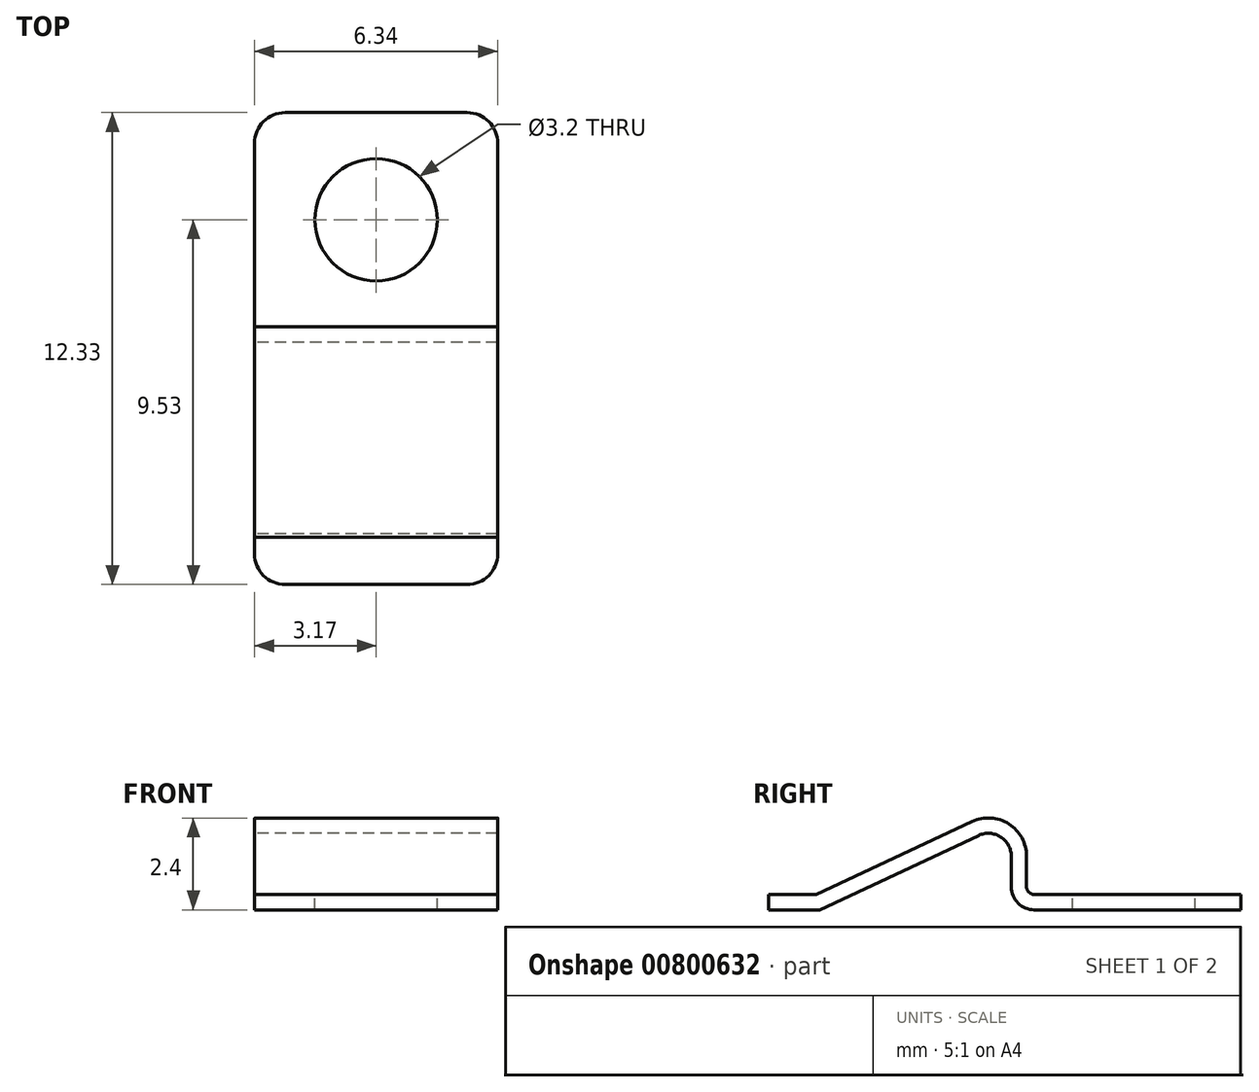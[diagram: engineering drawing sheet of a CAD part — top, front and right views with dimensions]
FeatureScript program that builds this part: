
annotation { "Feature Type Name" : "Feature", "Feature Type Description" : "" }
export const myFeature = defineFeature(function(context is Context, id is Id, definition is map)
    precondition{}
    {
        {
            var Q0;
            Q0=qCreatedBy(makeId("Right.planeOp"),FACE);
            var sketch = newSketch(context, id + "F0", { "sketchPlane" : qUnion([Q0])});
            skLineSegment(sketch, "E0", {"start": v(0, 0) * mm, "end": v(-5.4, 0) * mm});
            skLineSegment(sketch, "E1", {"start": v(-6, 0.6) * mm, "end": v(-6, 1.4) * mm});
            skLineSegment(sketch, "E2", {"start": v(-6.85, 1.94) * mm, "end": v(-11, 0) * mm});
            skLineSegment(sketch, "E3", {"start": v(-11, 0) * mm, "end": v(-12.33, 0) * mm});
            skLineSegment(sketch, "E4.0", {"start": v(0, 0.4) * mm, "end": v(-5.4, 0.4) * mm});
            skLineSegment(sketch, "E5.0", {"start": v(-5.6, 0.6) * mm, "end": v(-5.6, 1.4) * mm});
            skLineSegment(sketch, "E6.0", {"start": v(-7.02, 2.3) * mm, "end": v(-11.09, 0.4) * mm});
            skLineSegment(sketch, "E7.0", {"start": v(-11.09, 0.4) * mm, "end": v(-12.33, 0.4) * mm});
            skLineSegment(sketch, "E8", {"start": v(-12.33, 0) * mm, "end": v(-12.33, 0.4) * mm});
            skPoint(sketch, "E9.visualSharp", {"position": v(-6, 2.34) * mm});
            skArc(sketch, "E9.filletArc", {"start": v(-6, 1.4) * mm, "mid": v(-6.28, 1.9) * mm, "end": v(-6.85, 1.94) * mm});
            skArc(sketch, "E10.0", {"start": v(-5.6, 1.4) * mm, "mid": v(-6.06, 2.24) * mm, "end": v(-7.02, 2.3) * mm});
            skPoint(sketch, "E11.visualSharp", {"position": v(-5.6, 0.4) * mm});
            skArc(sketch, "E11.filletArc", {"start": v(-5.6, 0.6) * mm, "mid": v(-5.54, 0.46) * mm, "end": v(-5.4, 0.4) * mm});
            skPoint(sketch, "E12.visualSharp", {"position": v(-6, 0) * mm});
            skArc(sketch, "E12.filletArc", {"start": v(-6, 0.6) * mm, "mid": v(-5.82, 0.18) * mm, "end": v(-5.4, 0) * mm});
            skLineSegment(sketch, "E13", {"start": v(0, 0) * mm, "end": v(0, 0.4) * mm});
            skSolve(sketch);
        }
        {
            var Q0;
            Q0 = qSketchRegion(id + "F0", true);
            extrude(context, id + "F1", {"entities" : qUnion([Q0]), "endBound" : BoundingType.SYMMETRIC, "depth" : 6.35 * mm, "offsetDistance" : 25 * mm});
        }
        {
            var Q0;
            Q0=makeQuery(id+"F1.opExtrude","CAP_EDGE",EDGE,{"disambiguationData":[OSD([sQuery(id+"F0.wireOp",EDGE,"E8")])],"isStart":false});
            var Q1;
            Q1=makeQuery(id+"F1.opExtrude","CAP_EDGE",EDGE,{"disambiguationData":[OSD([sQuery(id+"F0.wireOp",EDGE,"E8")])],"isStart":true});
            var Q2;
            Q2=makeQuery(id+"F1.opExtrude","CAP_EDGE",EDGE,{"disambiguationData":[OSD([sQuery(id+"F0.wireOp",EDGE,"E13")])],"isStart":false});
            var Q3;
            Q3=makeQuery(id+"F1.opExtrude","CAP_EDGE",EDGE,{"disambiguationData":[OSD([sQuery(id+"F0.wireOp",EDGE,"E13")])],"isStart":true});
            fillet(context, id + "F2", {"entities" : qUnion([Q0, Q1, Q2, Q3]), "radius" : 0.8 * mm, "tangentPropagation" : true, "allowEdgeOverflow" : false});
        }
        {
            var Q0;
            Q0=makeQuery(id+"F1.opExtrude","SWEPT_FACE",FACE,{"disambiguationData":[OSD([sQuery(id+"F0.wireOp",EDGE,"E4.0")])]});
            var sketch = newSketch(context, id + "F3", { "sketchPlane" : qUnion([Q0])});
            skCircle(sketch, "E14", {"center": v(0, -2.8) * mm, "radius": 1.6 * mm});
            skSolve(sketch);
        }
        {
            var Q0;
            Q0=sQuery(id+"F3.wireOp",VERTEX,"E14.center");
            var Q1;
            Q1=makeQuery(id+"F1.opExtrude","SWEPT_BODY",BODY,{"disambiguationData":[OSD([sQuery(id+"F0.wireOp",EDGE,"E0"),sQuery(id+"F0.wireOp",EDGE,"E1"),sQuery(id+"F0.wireOp",EDGE,"E2"),sQuery(id+"F0.wireOp",EDGE,"E3"),sQuery(id+"F0.wireOp",EDGE,"E4.0"),sQuery(id+"F0.wireOp",EDGE,"E5.0"),sQuery(id+"F0.wireOp",EDGE,"E6.0"),sQuery(id+"F0.wireOp",EDGE,"E7.0"),sQuery(id+"F0.wireOp",EDGE,"E8"),sQuery(id+"F0.wireOp",EDGE,"E9.filletArc"),sQuery(id+"F0.wireOp",EDGE,"E10.0"),sQuery(id+"F0.wireOp",EDGE,"E11.filletArc"),sQuery(id+"F0.wireOp",EDGE,"E12.filletArc"),sQuery(id+"F0.wireOp",EDGE,"E13")])]});
            hole(context, id + "F4", {"style" : HoleStyle.SIMPLE, "endStyle" : HoleEndStyle.THROUGH, "holeDiameter" : 3.2 * mm, "majorDiameter" : 5 * mm, "isTappedThrough" : true, "tappedDepth" : 12 * mm, "tapClearance" : 3, "locations" : qUnion([Q0]), "scope" : qUnion([Q1])});
        }
    });
